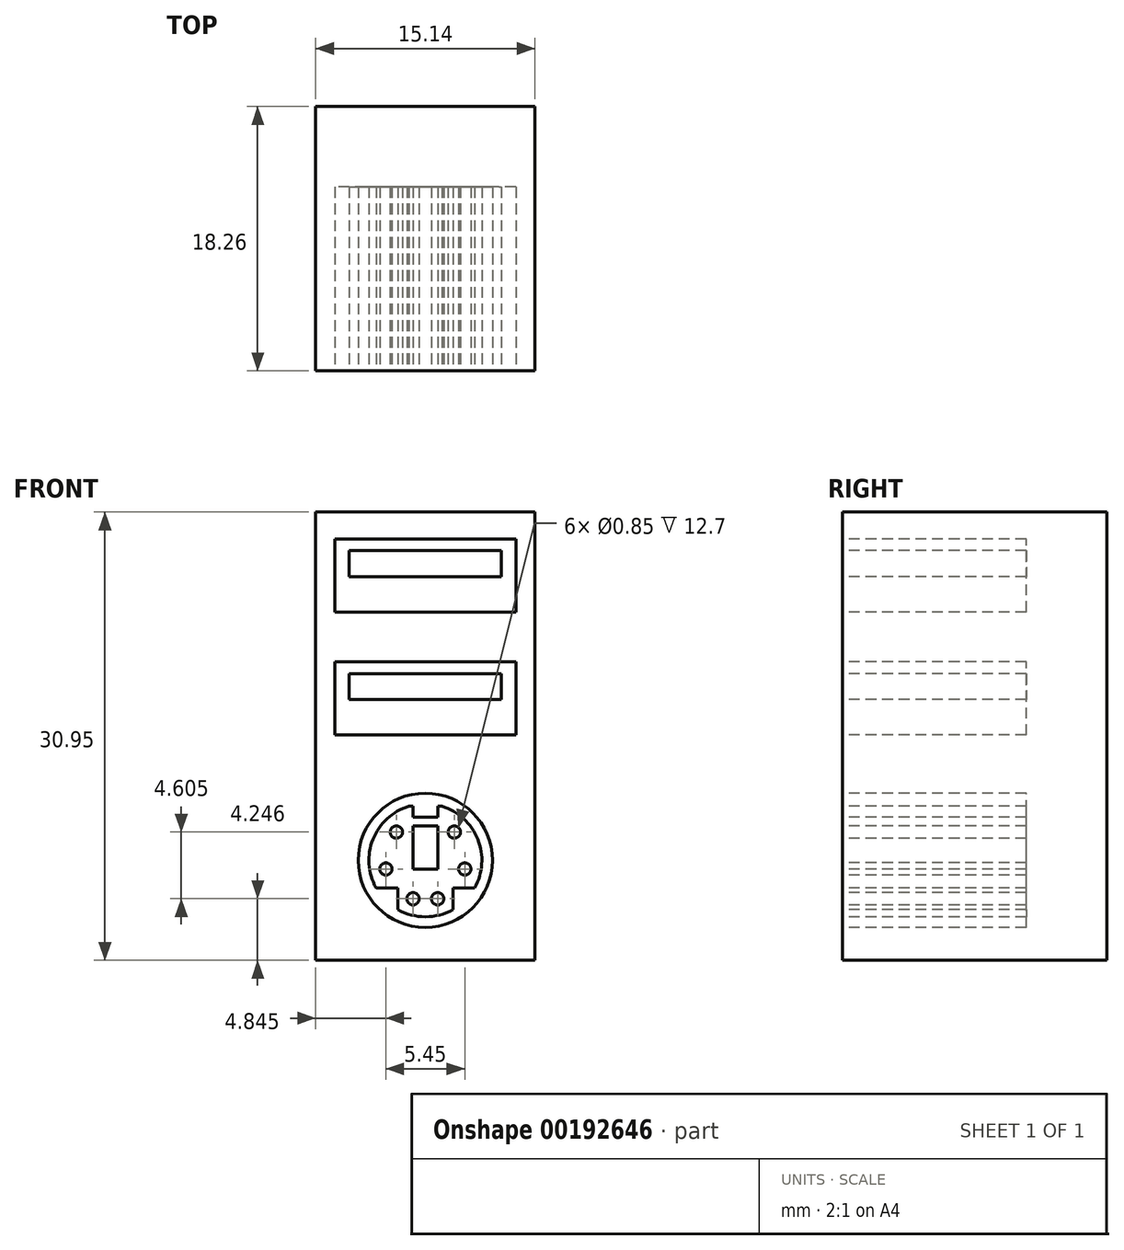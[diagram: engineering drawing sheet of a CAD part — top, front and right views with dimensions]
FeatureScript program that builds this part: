
annotation { "Feature Type Name" : "Feature", "Feature Type Description" : "" }
export const myFeature = defineFeature(function(context is Context, id is Id, definition is map)
    precondition{}
    {
        {
            var Q0;
            Q0=qCreatedBy(makeId("Top.planeOp"),FACE);
            var sketch = newSketch(context, id + "F0", { "sketchPlane" : qUnion([Q0])});
            skLineSegment(sketch, "E0.bottom", {"start": v(-7.57, 9.13) * mm, "end": v(7.57, 9.13) * mm});
            skLineSegment(sketch, "E0.top", {"start": v(-7.57, -9.13) * mm, "end": v(7.57, -9.13) * mm});
            skLineSegment(sketch, "E0.left", {"start": v(-7.57, 9.13) * mm, "end": v(-7.57, -9.13) * mm});
            skLineSegment(sketch, "E0.right", {"start": v(7.57, 9.13) * mm, "end": v(7.57, -9.13) * mm});
            skPoint(sketch, "E0.middle", {"position": v(0, 0) * mm});
            skSolve(sketch);
        }
        {
            var Q0;
            Q0 = qSketchRegion(id + "F0", true);
            extrude(context, id + "F3", {"entities" : qUnion([Q0]), "depth" : 30.95 * mm});
        }
        {
            var Q0;
            Q0=makeQuery(id+"F3.opExtrude","SWEPT_FACE",FACE,{"disambiguationData":[OSD([sQuery(id+"F0.wireOp",EDGE,"E0.top")])]});
            var sketch = newSketch(context, id + "F1", { "sketchPlane" : qUnion([Q0])});
            skLineSegment(sketch, "E1.bottom", {"start": v(6.25, 24.05) * mm, "end": v(-6.25, 24.05) * mm});
            skLineSegment(sketch, "E1.top", {"start": v(6.25, 29.1) * mm, "end": v(-6.25, 29.1) * mm});
            skLineSegment(sketch, "E1.left", {"start": v(6.25, 24.05) * mm, "end": v(6.25, 29.1) * mm});
            skLineSegment(sketch, "E1.right", {"start": v(-6.25, 24.05) * mm, "end": v(-6.25, 29.1) * mm});
            skPoint(sketch, "E1.middle", {"position": v(0, 26.57) * mm});
            skLineSegment(sketch, "E2.bottom", {"start": v(6.25, 15.55) * mm, "end": v(-6.25, 15.55) * mm});
            skLineSegment(sketch, "E2.top", {"start": v(6.25, 20.6) * mm, "end": v(-6.25, 20.6) * mm});
            skLineSegment(sketch, "E2.left", {"start": v(6.25, 15.55) * mm, "end": v(6.25, 20.6) * mm});
            skLineSegment(sketch, "E2.right", {"start": v(-6.25, 15.55) * mm, "end": v(-6.25, 20.6) * mm});
            skPoint(sketch, "E2.middle", {"position": v(0, 18.07) * mm});
            skCircle(sketch, "E3", {"center": v(0, 6.9) * mm, "radius": 4.63 * mm});
            skLineSegment(sketch, "E4.bottom", {"start": v(-5.25, 19.8) * mm, "end": v(5.25, 19.8) * mm});
            skLineSegment(sketch, "E4.top", {"start": v(-5.25, 18) * mm, "end": v(5.25, 18) * mm});
            skLineSegment(sketch, "E4.left", {"start": v(-5.25, 19.8) * mm, "end": v(-5.25, 18) * mm});
            skLineSegment(sketch, "E4.right", {"start": v(5.25, 19.8) * mm, "end": v(5.25, 18) * mm});
            skLineSegment(sketch, "E5.bottom", {"start": v(-5.25, 28.3) * mm, "end": v(5.25, 28.3) * mm});
            skLineSegment(sketch, "E5.top", {"start": v(-5.25, 26.5) * mm, "end": v(5.25, 26.5) * mm});
            skLineSegment(sketch, "E5.left", {"start": v(-5.25, 28.3) * mm, "end": v(-5.25, 26.5) * mm});
            skLineSegment(sketch, "E5.right", {"start": v(5.25, 28.3) * mm, "end": v(5.25, 26.5) * mm});
            skArc(sketch, "E6", {"start": v(-1.15, 10.63) * mm, "mid": v(-3.62, 8.35) * mm, "end": v(-3.4, 5) * mm});
            skLineSegment(sketch, "E7", {"start": v(-0.85, 9.88) * mm, "end": v(0.85, 9.88) * mm});
            skLineSegment(sketch, "E8", {"start": v(0.85, 9.88) * mm, "end": v(0.85, 10.63) * mm});
            skLineSegment(sketch, "E9", {"start": v(0.85, 10.63) * mm, "end": v(1.15, 10.63) * mm});
            skLineSegment(sketch, "E10", {"start": v(-0.85, 9.88) * mm, "end": v(-0.85, 10.63) * mm});
            skLineSegment(sketch, "E11", {"start": v(-0.85, 10.63) * mm, "end": v(-1.15, 10.63) * mm});
            skLineSegment(sketch, "E12", {"start": v(-3.4, 5) * mm, "end": v(-1.9, 5) * mm});
            skLineSegment(sketch, "E13", {"start": v(-1.9, 5) * mm, "end": v(-1.9, 3.5) * mm});
            skLineSegment(sketch, "E14", {"start": v(1.9, 3.5) * mm, "end": v(1.9, 5) * mm});
            skLineSegment(sketch, "E15", {"start": v(1.9, 5) * mm, "end": v(3.4, 5) * mm});
            skArc(sketch, "E16.trimOffspring", {"start": v(-1.9, 3.5) * mm, "mid": v(0, 3) * mm, "end": v(1.9, 3.5) * mm});
            skArc(sketch, "E17.trimOffspring", {"start": v(3.4, 5) * mm, "mid": v(3.62, 8.35) * mm, "end": v(1.15, 10.63) * mm});
            skCircle(sketch, "E18", {"center": v(-0.85, 4.25) * mm, "radius": 0.42 * mm});
            skCircle(sketch, "E19", {"center": v(0.85, 4.25) * mm, "radius": 0.42 * mm});
            skCircle(sketch, "E20", {"center": v(-2.72, 6.3) * mm, "radius": 0.42 * mm});
            skCircle(sketch, "E21", {"center": v(2.72, 6.3) * mm, "radius": 0.42 * mm});
            skCircle(sketch, "E22", {"center": v(-2, 8.85) * mm, "radius": 0.42 * mm});
            skCircle(sketch, "E23", {"center": v(2, 8.85) * mm, "radius": 0.42 * mm});
            skLineSegment(sketch, "E24.bottom", {"start": v(-0.85, 6.3) * mm, "end": v(0.85, 6.3) * mm});
            skLineSegment(sketch, "E24.top", {"start": v(-0.85, 9.28) * mm, "end": v(0.85, 9.28) * mm});
            skLineSegment(sketch, "E24.left", {"start": v(-0.85, 6.3) * mm, "end": v(-0.85, 9.28) * mm});
            skLineSegment(sketch, "E24.right", {"start": v(0.85, 6.3) * mm, "end": v(0.85, 9.28) * mm});
            skPoint(sketch, "E24.middle", {"position": v(0, 7.79) * mm});
            skLineSegment(sketch, "E25", {"start": v(-1.9, 4.25) * mm, "end": v(1.9, 4.25) * mm, "construction": true});
            skCircle(sketch, "E26", {"center": v(0, 6.9) * mm, "radius": 2.8 * mm, "construction": true});
            skSolve(sketch);
        }
        {
            var Q0;
            Q0 = qSketchRegion(id + "F1", true);
            extrude(context, id + "F4", {"entities" : qUnion([Q0]), "operationType" : NewBodyOperationType.REMOVE, "oppositeDirection" : true, "depth" : 12.7 * mm});
        }
        {
            var Q0;
            Q0=makeQuery(id+"F1.imprint","IMPRINT",FACE,{"disambiguationData":[TD([[makeQuery(id+"F1.imprint","IMPRINT",EDGE,{"derivedFrom":sQuery(id+"F1.wireOp",EDGE,"E22")}),1.0]])]});
            var Q1;
            Q1=makeQuery(id+"F1.imprint","IMPRINT",FACE,{"disambiguationData":[TD([[makeQuery(id+"F1.imprint","IMPRINT",EDGE,{"derivedFrom":sQuery(id+"F1.wireOp",EDGE,"E20")}),1.0]])]});
            var Q2;
            Q2=makeQuery(id+"F1.imprint","IMPRINT",FACE,{"disambiguationData":[TD([[makeQuery(id+"F1.imprint","IMPRINT",EDGE,{"derivedFrom":sQuery(id+"F1.wireOp",EDGE,"E18")}),1.0]])]});
            var Q3;
            Q3=makeQuery(id+"F1.imprint","IMPRINT",FACE,{"disambiguationData":[TD([[makeQuery(id+"F1.imprint","IMPRINT",EDGE,{"derivedFrom":sQuery(id+"F1.wireOp",EDGE,"E21")}),1.0]])]});
            var Q4;
            Q4=makeQuery(id+"F1.imprint","IMPRINT",FACE,{"disambiguationData":[TD([[makeQuery(id+"F1.imprint","IMPRINT",EDGE,{"derivedFrom":sQuery(id+"F1.wireOp",EDGE,"E23")}),1.0]])]});
            var Q5;
            Q5=makeQuery(id+"F1.imprint","IMPRINT",FACE,{"disambiguationData":[TD([[makeQuery(id+"F1.imprint","IMPRINT",EDGE,{"derivedFrom":sQuery(id+"F1.wireOp",EDGE,"E19")}),1.0]])]});
            var Q6;
            Q6=makeQuery(id+"F1.imprint","IMPRINT",FACE,{"disambiguationData":[TD([[makeQuery(id+"F1.imprint","IMPRINT",EDGE,{"derivedFrom":sQuery(id+"F1.wireOp",EDGE,"E24.bottom")}),1.0]])]});
            extrude(context, id + "F2", {"entities" : qUnion([Q0, Q1, Q2, Q3, Q4, Q5, Q6]), "operationType" : NewBodyOperationType.REMOVE, "oppositeDirection" : true, "depth" : 12.7 * mm});
        }
    });
